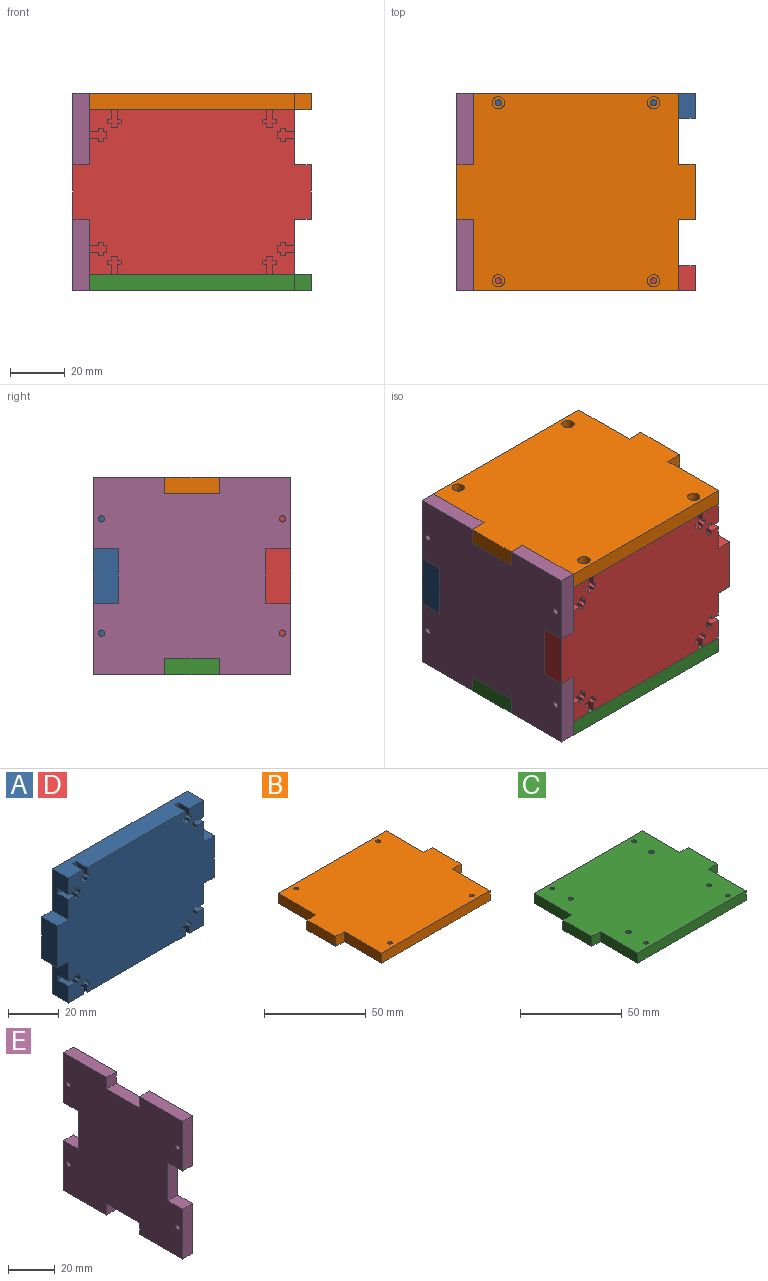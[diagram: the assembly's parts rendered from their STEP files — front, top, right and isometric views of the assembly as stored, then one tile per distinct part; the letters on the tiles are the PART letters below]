
ASSEMBLY  parts=5 mates=8
PART A: 110 faces, bbox 87x9x60 mm
  f0: plane 75x9mm, normal (0,0,-1), area 647.6mm2, adj f1,f3,f4,f13,f62,f63,f73,f74
  f1: plane 20x9mm, normal (1,0,0), area 166.3mm2, adj f0,f3,f5,f13,f50,f60,f61
  f2: plane 20x9mm, normal (1,0,0), area 166.3mm2, adj f3,f7,f8,f13,f38,f39,f49
  f3: plane 87x60mm, normal (0,-1,0), area 4589.1mm2, adj f0,f1,f2,f4,f5,f6,f7,f8
  f4: plane 20x9mm, normal (-1,0,0), area 166.3mm2, adj f0,f3,f12,f13,f86,f96,f97
  f5: plane 9x6mm, normal (0,0,-1), area 54mm2, adj f1,f3,f6,f13
  f6: plane 20x9mm, normal (1,0,0), area 180mm2, adj f3,f5,f7,f13
  f7: plane 9x6mm, normal (0,0,1), area 54mm2, adj f2,f3,f6,f13
  f8: plane 75x9mm, normal (0,0,1), area 647.6mm2, adj f2,f3,f9,f13,f26,f36,f37,f98
  f9: plane 20x9mm, normal (-1,0,0), area 166.3mm2, adj f3,f8,f10,f13,f14,f15,f25
  f10: plane 9x6mm, normal (0,0,1), area 54mm2, adj f3,f9,f11,f13
  f11: plane 20x9mm, normal (-1,0,0), area 180mm2, adj f3,f10,f12,f13
  f12: plane 9x6mm, normal (0,0,-1), area 54mm2, adj f3,f4,f11,f13
  f13: plane 87x60mm, normal (0,1,0), area 4740mm2, adj f0,f1,f2,f4,f5,f6,f7,f8
  f14: plane 6x3.4mm, normal (0,0,-1), area 20.4mm2, adj f3,f9,f24,f25
  f15: plane 6x3.4mm, normal (0,0,1), area 20.4mm2, adj f3,f9,f16,f25
  f16: plane 6x1.36mm, normal (1,0,0), area 8.1mm2, adj f3,f15,f17,f25
  f17: plane 6x1.6mm, normal (0,0,1), area 9.6mm2, adj f3,f16,f18,f25
  f18: plane 6x1.36mm, normal (-1,0,0), area 8.1mm2, adj f3,f17,f19,f25
  f19: plane 6x1.35mm, normal (0,0,1), area 8.1mm2, adj f3,f18,f20,f25
  f20: plane 6x2.29mm, normal (-1,0,0), area 13.7mm2, adj f3,f19,f21,f25
  f21: plane 6x1.35mm, normal (0,0,-1), area 8.1mm2, adj f3,f20,f22,f25
  f22: plane 6x1.36mm, normal (-1,0,0), area 8.1mm2, adj f3,f21,f23,f25
  f23: plane 6x1.6mm, normal (0,0,-1), area 9.6mm2, adj f3,f22,f24,f25
  f24: plane 6x1.36mm, normal (1,0,0), area 8.1mm2, adj f3,f14,f23,f25
  f25: plane 6.35x5mm, normal (0,-1,0), area 18.9mm2, adj f9,f14,f15,f16,f17,f18,f19,f20
  f26: plane 6x3.4mm, normal (1,0,0), area 20.4mm2, adj f3,f8,f27,f37
  f27: plane 6x1.36mm, normal (0,0,-1), area 8.1mm2, adj f3,f26,f28,f37
  f28: plane 6x1.6mm, normal (1,0,0), area 9.6mm2, adj f3,f27,f29,f37
  f29: plane 6x1.36mm, normal (0,0,1), area 8.1mm2, adj f3,f28,f30,f37
  f30: plane 6x1.35mm, normal (1,0,0), area 8.1mm2, adj f3,f29,f31,f37
  f31: plane 6x2.29mm, normal (0,0,1), area 13.7mm2, adj f3,f30,f32,f37
  f32: plane 6x1.35mm, normal (-1,0,0), area 8.1mm2, adj f3,f31,f33,f37
  f33: plane 6x1.36mm, normal (0,0,1), area 8.1mm2, adj f3,f32,f34,f37
  f34: plane 6x1.6mm, normal (-1,0,0), area 9.6mm2, adj f3,f33,f35,f37
  f35: plane 6x1.36mm, normal (0,0,-1), area 8.1mm2, adj f3,f34,f36,f37
  f36: plane 6x3.4mm, normal (-1,0,0), area 20.4mm2, adj f3,f8,f35,f37
  f37: plane 6.35x5mm, normal (0,-1,0), area 18.9mm2, adj f8,f26,f27,f28,f29,f30,f31,f32
  f38: plane 6x3.4mm, normal (0,0,1), area 20.4mm2, adj f2,f3,f48,f49
  f39: plane 6x3.4mm, normal (0,0,-1), area 20.4mm2, adj f2,f3,f40,f49
  f40: plane 6x1.36mm, normal (-1,0,0), area 8.1mm2, adj f3,f39,f41,f49
  f41: plane 6x1.6mm, normal (0,0,-1), area 9.6mm2, adj f3,f40,f42,f49
  f42: plane 6x1.36mm, normal (1,0,0), area 8.1mm2, adj f3,f41,f43,f49
  f43: plane 6x1.35mm, normal (0,0,-1), area 8.1mm2, adj f3,f42,f44,f49
  f44: plane 6x2.29mm, normal (1,0,0), area 13.7mm2, adj f3,f43,f45,f49
  f45: plane 6x1.35mm, normal (0,0,1), area 8.1mm2, adj f3,f44,f46,f49
  f46: plane 6x1.36mm, normal (1,0,0), area 8.1mm2, adj f3,f45,f47,f49
  f47: plane 6x1.6mm, normal (0,0,1), area 9.6mm2, adj f3,f46,f48,f49
  f48: plane 6x1.36mm, normal (-1,0,0), area 8.1mm2, adj f3,f38,f47,f49
  f49: plane 6.35x5mm, normal (0,-1,0), area 18.9mm2, adj f2,f38,f39,f40,f41,f42,f43,f44
  f50: plane 6x3.4mm, normal (0,0,-1), area 20.4mm2, adj f1,f3,f51,f61
  f51: plane 6x1.36mm, normal (-1,0,0), area 8.1mm2, adj f3,f50,f52,f61
  f52: plane 6x1.6mm, normal (0,0,-1), area 9.6mm2, adj f3,f51,f53,f61
  f53: plane 6x1.36mm, normal (1,0,0), area 8.1mm2, adj f3,f52,f54,f61
  f54: plane 6x1.35mm, normal (0,0,-1), area 8.1mm2, adj f3,f53,f55,f61
  f55: plane 6x2.29mm, normal (1,0,0), area 13.7mm2, adj f3,f54,f56,f61
  f56: plane 6x1.35mm, normal (0,0,1), area 8.1mm2, adj f3,f55,f57,f61
  f57: plane 6x1.36mm, normal (1,0,0), area 8.1mm2, adj f3,f56,f58,f61
  f58: plane 6x1.6mm, normal (0,0,1), area 9.6mm2, adj f3,f57,f59,f61
  f59: plane 6x1.36mm, normal (-1,0,0), area 8.1mm2, adj f3,f58,f60,f61
  f60: plane 6x3.4mm, normal (0,0,1), area 20.4mm2, adj f1,f3,f59,f61
  f61: plane 6.35x5mm, normal (0,-1,0), area 18.9mm2, adj f1,f50,f51,f52,f53,f54,f55,f56
  f62: plane 6x3.4mm, normal (1,0,0), area 20.4mm2, adj f0,f3,f72,f73
  f63: plane 6x3.4mm, normal (-1,0,0), area 20.4mm2, adj f0,f3,f64,f73
  f64: plane 6x1.36mm, normal (0,0,1), area 8.1mm2, adj f3,f63,f65,f73
  f65: plane 6x1.6mm, normal (-1,0,0), area 9.6mm2, adj f3,f64,f66,f73
  f66: plane 6x1.36mm, normal (0,0,-1), area 8.1mm2, adj f3,f65,f67,f73
  f67: plane 6x1.35mm, normal (-1,0,0), area 8.1mm2, adj f3,f66,f68,f73
  f68: plane 6x2.29mm, normal (0,0,-1), area 13.7mm2, adj f3,f67,f69,f73
  f69: plane 6x1.35mm, normal (1,0,0), area 8.1mm2, adj f3,f68,f70,f73
  f70: plane 6x1.36mm, normal (0,0,-1), area 8.1mm2, adj f3,f69,f71,f73
  f71: plane 6x1.6mm, normal (1,0,0), area 9.6mm2, adj f3,f70,f72,f73
  f72: plane 6x1.36mm, normal (0,0,1), area 8.1mm2, adj f3,f62,f71,f73
  f73: plane 6.35x5mm, normal (0,-1,0), area 18.9mm2, adj f0,f62,f63,f64,f65,f66,f67,f68
  f74: plane 6x3.4mm, normal (1,0,0), area 20.4mm2, adj f0,f3,f84,f85
  f75: plane 6x3.4mm, normal (-1,0,0), area 20.4mm2, adj f0,f3,f76,f85
  f76: plane 6x1.36mm, normal (0,0,1), area 8.1mm2, adj f3,f75,f77,f85
  f77: plane 6x1.6mm, normal (-1,0,0), area 9.6mm2, adj f3,f76,f78,f85
  f78: plane 6x1.36mm, normal (0,0,-1), area 8.1mm2, adj f3,f77,f79,f85
  f79: plane 6x1.35mm, normal (-1,0,0), area 8.1mm2, adj f3,f78,f80,f85
  f80: plane 6x2.29mm, normal (0,0,-1), area 13.7mm2, adj f3,f79,f81,f85
  f81: plane 6x1.35mm, normal (1,0,0), area 8.1mm2, adj f3,f80,f82,f85
  f82: plane 6x1.36mm, normal (0,0,-1), area 8.1mm2, adj f3,f81,f83,f85
  f83: plane 6x1.6mm, normal (1,0,0), area 9.6mm2, adj f3,f82,f84,f85
  f84: plane 6x1.36mm, normal (0,0,1), area 8.1mm2, adj f3,f74,f83,f85
  f85: plane 6.35x5mm, normal (0,-1,0), area 18.9mm2, adj f0,f74,f75,f76,f77,f78,f79,f80
  f86: plane 6x3.4mm, normal (0,0,1), area 20.4mm2, adj f3,f4,f87,f97
  f87: plane 6x1.36mm, normal (1,0,0), area 8.1mm2, adj f3,f86,f88,f97
  f88: plane 6x1.6mm, normal (0,0,1), area 9.6mm2, adj f3,f87,f89,f97
  f89: plane 6x1.36mm, normal (-1,0,0), area 8.1mm2, adj f3,f88,f90,f97
  f90: plane 6x1.35mm, normal (0,0,1), area 8.1mm2, adj f3,f89,f91,f97
  f91: plane 6x2.29mm, normal (-1,0,0), area 13.7mm2, adj f3,f90,f92,f97
  f92: plane 6x1.35mm, normal (0,0,-1), area 8.1mm2, adj f3,f91,f93,f97
  f93: plane 6x1.36mm, normal (-1,0,0), area 8.1mm2, adj f3,f92,f94,f97
  f94: plane 6x1.6mm, normal (0,0,-1), area 9.6mm2, adj f3,f93,f95,f97
  f95: plane 6x1.36mm, normal (1,0,0), area 8.1mm2, adj f3,f94,f96,f97
  f96: plane 6x3.4mm, normal (0,0,-1), area 20.4mm2, adj f3,f4,f95,f97
  f97: plane 6.35x5mm, normal (0,-1,0), area 18.9mm2, adj f4,f86,f87,f88,f89,f90,f91,f92
  f98: plane 6x3.4mm, normal (1,0,0), area 20.4mm2, adj f3,f8,f99,f109
  f99: plane 6x1.36mm, normal (0,0,-1), area 8.1mm2, adj f3,f98,f100,f109
  f100: plane 6x1.6mm, normal (1,0,0), area 9.6mm2, adj f3,f99,f101,f109
  f101: plane 6x1.36mm, normal (0,0,1), area 8.1mm2, adj f3,f100,f102,f109
  f102: plane 6x1.35mm, normal (1,0,0), area 8.1mm2, adj f3,f101,f103,f109
  f103: plane 6x2.29mm, normal (0,0,1), area 13.7mm2, adj f3,f102,f104,f109
  f104: plane 6x1.35mm, normal (-1,0,0), area 8.1mm2, adj f3,f103,f105,f109
  f105: plane 6x1.36mm, normal (0,0,1), area 8.1mm2, adj f3,f104,f106,f109
  f106: plane 6x1.6mm, normal (-1,0,0), area 9.6mm2, adj f3,f105,f107,f109
  f107: plane 6x1.36mm, normal (0,0,-1), area 8.1mm2, adj f3,f106,f108,f109
  f108: plane 6x3.4mm, normal (-1,0,0), area 20.4mm2, adj f3,f8,f107,f109
  f109: plane 6.35x5mm, normal (0,-1,0), area 18.9mm2, adj f8,f98,f99,f100,f101,f102,f103,f104
PART B: 26 faces, bbox 87x72x6 mm
  f0: plane 87x72mm, normal (0,0,1), area 5623.6mm2, adj f2,f3,f4,f5,f6,f7,f8,f9
  f1: plane 87x72mm, normal (0,0,-1), area 5576.4mm2, adj f2,f3,f4,f5,f6,f7,f8,f9
  f2: plane 6x6mm, normal (0,1,0), area 36mm2, adj f0,f1,f3,f13
  f3: plane 26x6mm, normal (1,0,0), area 156mm2, adj f0,f1,f2,f4
  f4: plane 75x6mm, normal (0,1,0), area 450mm2, adj f0,f1,f3,f5
  f5: plane 26x6mm, normal (-1,0,0), area 156mm2, adj f0,f1,f4,f6
  f6: plane 6x6mm, normal (0,1,0), area 36mm2, adj f0,f1,f5,f7
  f7: plane 20x6mm, normal (-1,0,0), area 120mm2, adj f0,f1,f6,f8
  f8: plane 6x6mm, normal (0,-1,0), area 36mm2, adj f0,f1,f7,f9
  f9: plane 26x6mm, normal (-1,0,0), area 156mm2, adj f0,f1,f8,f10
  f10: plane 75x6mm, normal (0,-1,0), area 450mm2, adj f0,f1,f9,f11
  f11: plane 26x6mm, normal (1,0,0), area 156mm2, adj f0,f1,f10,f12
  f12: plane 6x6mm, normal (0,-1,0), area 36mm2, adj f0,f1,f11,f13
  f13: plane 20x6mm, normal (1,0,0), area 120mm2, adj f0,f1,f2,f12
  f14: cylinder r=2.25mm len=4.5mm, axis (0,0,-1), area 42.4mm2, adj f1,f15
  f15: plane 4.5x4.5mm, normal (0,0,-1), area 11.8mm2, adj f14,f25
  f16: cylinder r=2.25mm len=4.5mm, axis (0,0,-1), area 42.4mm2, adj f1,f17
  f17: plane 4.5x4.5mm, normal (0,0,-1), area 11.8mm2, adj f16,f24
  f18: cylinder r=2.25mm len=4.5mm, axis (0,0,-1), area 42.4mm2, adj f1,f19
  f19: plane 4.5x4.5mm, normal (0,0,-1), area 11.8mm2, adj f18,f23
  f20: cylinder r=2.25mm len=4.5mm, axis (0,0,-1), area 42.4mm2, adj f1,f21
  f21: plane 4.5x4.5mm, normal (0,0,-1), area 11.8mm2, adj f20,f22
  f22: cylinder r=1.14mm len=3mm, axis (0,0,-1), area 21.5mm2, adj f0,f21
  f23: cylinder r=1.14mm len=3mm, axis (0,0,-1), area 21.5mm2, adj f0,f19
  f24: cylinder r=1.14mm len=3mm, axis (0,0,-1), area 21.5mm2, adj f0,f17
  f25: cylinder r=1.14mm len=3mm, axis (0,0,-1), area 21.5mm2, adj f0,f15
PART C: 38 faces, bbox 87x72x6 mm
  f0: plane 87x72mm, normal (0,0,1), area 5603.9mm2, adj f2,f3,f4,f5,f6,f7,f8,f9
  f1: plane 87x72mm, normal (0,0,-1), area 5512.8mm2, adj f2,f3,f4,f5,f6,f7,f8,f9
  f2: plane 6x6mm, normal (0,1,0), area 36mm2, adj f0,f1,f3,f13
  f3: plane 26x6mm, normal (1,0,0), area 156mm2, adj f0,f1,f2,f4
  f4: plane 75x6mm, normal (0,1,0), area 450mm2, adj f0,f1,f3,f5
  f5: plane 26x6mm, normal (-1,0,0), area 156mm2, adj f0,f1,f4,f6
  f6: plane 6x6mm, normal (0,1,0), area 36mm2, adj f0,f1,f5,f7
  f7: plane 20x6mm, normal (-1,0,0), area 120mm2, adj f0,f1,f6,f8
  f8: plane 6x6mm, normal (0,-1,0), area 36mm2, adj f0,f1,f7,f9
  f9: plane 26x6mm, normal (-1,0,0), area 156mm2, adj f0,f1,f8,f10
  f10: plane 75x6mm, normal (0,-1,0), area 450mm2, adj f0,f1,f9,f11
  f11: plane 26x6mm, normal (1,0,0), area 156mm2, adj f0,f1,f10,f12
  f12: plane 6x6mm, normal (0,-1,0), area 36mm2, adj f0,f1,f11,f13
  f13: plane 20x6mm, normal (1,0,0), area 120mm2, adj f0,f1,f2,f12
  f14: cylinder r=2.25mm len=4.5mm, axis (0,0,-1), area 42.4mm2, adj f1,f15
  f15: plane 4.5x4.5mm, normal (0,0,-1), area 11mm2, adj f14,f37
  f16: cylinder r=2.25mm len=4.5mm, axis (0,0,-1), area 42.4mm2, adj f1,f17
  f17: plane 4.5x4.5mm, normal (0,0,-1), area 11mm2, adj f16,f36
  f18: cylinder r=2.25mm len=4.5mm, axis (0,0,-1), area 42.4mm2, adj f1,f19
  f19: plane 4.5x4.5mm, normal (0,0,-1), area 11.8mm2, adj f18,f35
  f20: cylinder r=2.25mm len=4.5mm, axis (0,0,-1), area 42.4mm2, adj f1,f21
  f21: plane 4.5x4.5mm, normal (0,0,-1), area 11.8mm2, adj f20,f34
  f22: cylinder r=2.25mm len=4.5mm, axis (0,0,-1), area 42.4mm2, adj f1,f23
  f23: plane 4.5x4.5mm, normal (0,0,-1), area 11.8mm2, adj f22,f33
  f24: cylinder r=2.25mm len=4.5mm, axis (0,0,-1), area 42.4mm2, adj f1,f25
  f25: plane 4.5x4.5mm, normal (0,0,-1), area 11.8mm2, adj f24,f32
  f26: cylinder r=2.25mm len=4.5mm, axis (0,0,-1), area 42.4mm2, adj f1,f27
  f27: plane 4.5x4.5mm, normal (0,0,-1), area 11mm2, adj f26,f31
  f28: cylinder r=2.25mm len=4.5mm, axis (0,0,-1), area 42.4mm2, adj f1,f29
  f29: plane 4.5x4.5mm, normal (0,0,-1), area 11mm2, adj f28,f30
  f30: cylinder r=1.25mm len=3mm, axis (0,0,-1), area 23.6mm2, adj f0,f29
  f31: cylinder r=1.25mm len=3mm, axis (0,0,-1), area 23.6mm2, adj f0,f27
  f32: cylinder r=1.14mm len=3mm, axis (0,0,-1), area 21.5mm2, adj f0,f25
  f33: cylinder r=1.14mm len=3mm, axis (0,0,-1), area 21.5mm2, adj f0,f23
  f34: cylinder r=1.14mm len=3mm, axis (0,0,-1), area 21.5mm2, adj f0,f21
  f35: cylinder r=1.14mm len=3mm, axis (0,0,-1), area 21.5mm2, adj f0,f19
  f36: cylinder r=1.25mm len=3mm, axis (0,0,-1), area 23.6mm2, adj f0,f17
  f37: cylinder r=1.25mm len=3mm, axis (0,0,-1), area 23.6mm2, adj f0,f15
PART D: same geometry as A
PART E: 34 faces, bbox 6x72x72 mm
  f0: plane 72x72mm, normal (-1,0,0), area 4567.6mm2, adj f2,f3,f4,f5,f6,f7,f8,f9
  f1: plane 72x72mm, normal (1,0,0), area 4520.4mm2, adj f2,f3,f4,f5,f6,f7,f8,f9
  f2: plane 26x6mm, normal (0,1,0), area 156mm2, adj f0,f1,f9,f20
  f3: plane 26x6mm, normal (0,0,1), area 156mm2, adj f0,f1,f8,f12
  f4: plane 26x6mm, normal (0,-1,0), area 156mm2, adj f0,f1,f5,f13
  f5: plane 26x6mm, normal (0,0,-1), area 156mm2, adj f0,f1,f4,f17
  f6: plane 26x6mm, normal (0,1,0), area 156mm2, adj f0,f1,f7,f21
  f7: plane 26x6mm, normal (0,0,1), area 156mm2, adj f0,f1,f6,f11
  f8: plane 26x6mm, normal (0,-1,0), area 156mm2, adj f0,f1,f3,f14
  f9: plane 26x6mm, normal (0,0,-1), area 156mm2, adj f0,f1,f2,f16
  f10: plane 20x6mm, normal (0,0,1), area 120mm2, adj f0,f1,f11,f12
  f11: plane 6x6mm, normal (0,-1,0), area 36mm2, adj f0,f1,f7,f10
  f12: plane 6x6mm, normal (0,1,0), area 36mm2, adj f0,f1,f3,f10
  f13: plane 9x6mm, normal (0,0,1), area 54mm2, adj f0,f1,f4,f15
  f14: plane 9x6mm, normal (0,0,-1), area 54mm2, adj f0,f1,f8,f15
  f15: plane 20x6mm, normal (0,-1,0), area 120mm2, adj f0,f1,f13,f14
  f16: plane 6x6mm, normal (0,-1,0), area 36mm2, adj f0,f1,f9,f18
  f17: plane 6x6mm, normal (0,1,0), area 36mm2, adj f0,f1,f5,f18
  f18: plane 20x6mm, normal (0,0,-1), area 120mm2, adj f0,f1,f16,f17
  f19: plane 20x6mm, normal (0,1,0), area 120mm2, adj f0,f1,f20,f21
  f20: plane 9x6mm, normal (0,0,1), area 54mm2, adj f0,f1,f2,f19
  f21: plane 9x6mm, normal (0,0,-1), area 54mm2, adj f0,f1,f6,f19
  f22: cylinder r=2.25mm len=4.5mm, axis (1,0,0), area 42.4mm2, adj f1,f23
  f23: plane 4.5x4.5mm, normal (1,0,0), area 11.8mm2, adj f22,f32
  f24: cylinder r=2.25mm len=4.5mm, axis (1,0,0), area 42.4mm2, adj f1,f25
  f25: plane 4.5x4.5mm, normal (1,0,0), area 11.8mm2, adj f24,f30
  f26: cylinder r=2.25mm len=4.5mm, axis (1,0,0), area 42.4mm2, adj f1,f27
  f27: plane 4.5x4.5mm, normal (1,0,0), area 11.8mm2, adj f26,f31
  f28: cylinder r=2.25mm len=4.5mm, axis (1,0,0), area 42.4mm2, adj f1,f29
  f29: plane 4.5x4.5mm, normal (1,0,0), area 11.8mm2, adj f28,f33
  f30: cylinder r=1.14mm len=3mm, axis (1,0,0), area 21.5mm2, adj f0,f25
  f31: cylinder r=1.14mm len=3mm, axis (1,0,0), area 21.5mm2, adj f0,f27
  f32: cylinder r=1.14mm len=3mm, axis (1,0,0), area 21.5mm2, adj f0,f23
  f33: cylinder r=1.14mm len=3mm, axis (1,0,0), area 21.5mm2, adj f0,f29
PLACE A rot(axis=(0,0,1),180deg) t=(0,36,36)mm
PLACE B rot(axis=(1,0,0),180deg) t=(0,0,72)mm
PLACE C at identity
PLACE D t=(0,-36,36)mm
PLACE E t=(-43.5,0,36)mm
MATE planar B.f7 <-> D.f11  axis (-1,0,0) through (-43.5,0,69)mm
MATE planar B.f4 <-> C.f10  axis (0,-1,0) through (0,-36,69)mm
MATE fastened B.f0 <-> D.f8  axis (0,0,-1) through (0,-36,66)mm
MATE fastened A.f0 <-> C.f0  axis (0,0,-1) through (0,36,6)mm
MATE fastened E.f15 <-> D.f13  axis (0,-1,0) through (-43.5,-27,36)mm
MATE planar B.f13 <-> C.f13  axis (1,0,0) through (43.5,0,69)mm
MATE planar D.f3 <-> C.f10  axis (0,-1,0) through (0,-36,36)mm
MATE fastened D.f0 <-> C.f0  axis (0,0,-1) through (0,-36,6)mm
